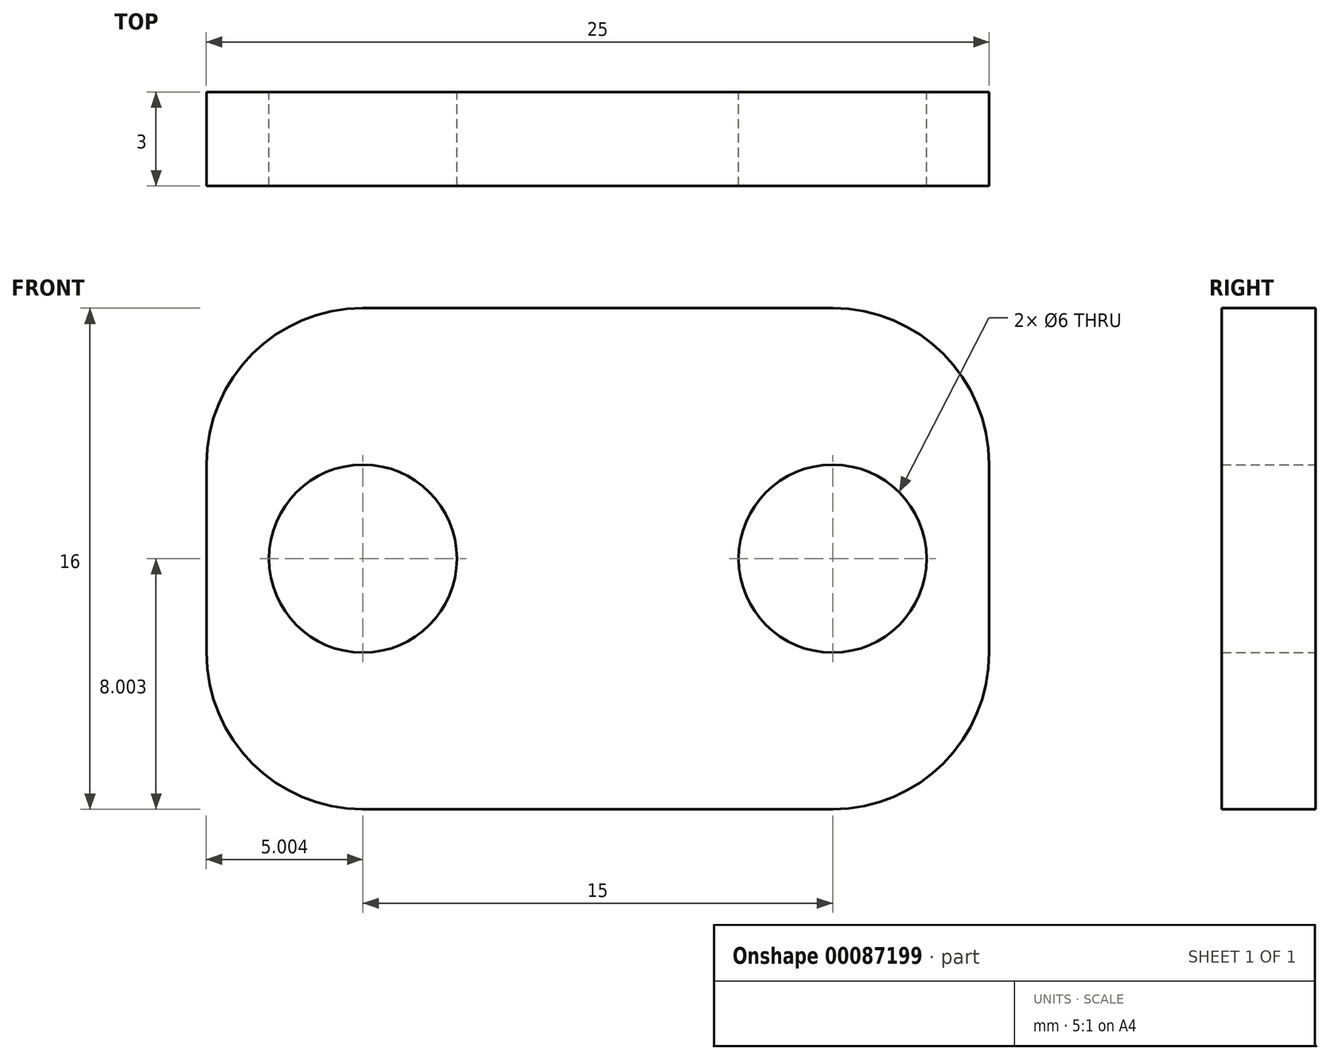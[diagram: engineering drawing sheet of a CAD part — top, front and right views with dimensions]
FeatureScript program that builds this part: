
annotation { "Feature Type Name" : "Feature", "Feature Type Description" : "" }
export const myFeature = defineFeature(function(context is Context, id is Id, definition is map)
    precondition{}
    {
        {
            var Q0;
            Q0=qCreatedBy(makeId("Front.planeOp"),FACE);
            var sketch = newSketch(context, id + "F0", { "sketchPlane" : qUnion([Q0])});
            skLineSegment(sketch, "E0", {"start": v(-155.44, 33.38) * mm, "end": v(-140.44, 33.38) * mm, "construction": true});
            skCircle(sketch, "E1", {"center": v(-155.44, 33.38) * mm, "radius": 3 * mm});
            skCircle(sketch, "E2", {"center": v(-140.44, 33.38) * mm, "radius": 3 * mm});
            skLineSegment(sketch, "E3.bottom", {"start": v(-140.44, 41.38) * mm, "end": v(-155.44, 41.38) * mm});
            skLineSegment(sketch, "E3.top", {"start": v(-140.44, 25.38) * mm, "end": v(-155.44, 25.38) * mm});
            skLineSegment(sketch, "E3.left", {"start": v(-135.44, 36.38) * mm, "end": v(-135.44, 30.38) * mm});
            skLineSegment(sketch, "E3.right", {"start": v(-160.44, 36.38) * mm, "end": v(-160.44, 30.38) * mm});
            skPoint(sketch, "E3.middle", {"position": v(-147.94, 33.38) * mm});
            skPoint(sketch, "E4.visualSharp", {"position": v(-135.44, 41.38) * mm});
            skArc(sketch, "E4.filletArc", {"start": v(-135.44, 36.38) * mm, "mid": v(-136.9, 39.92) * mm, "end": v(-140.44, 41.38) * mm});
            skPoint(sketch, "E5.visualSharp", {"position": v(-135.44, 25.38) * mm});
            skArc(sketch, "E5.filletArc", {"start": v(-140.44, 25.38) * mm, "mid": v(-136.9, 26.85) * mm, "end": v(-135.44, 30.38) * mm});
            skPoint(sketch, "E6.visualSharp", {"position": v(-160.44, 25.38) * mm});
            skArc(sketch, "E6.filletArc", {"start": v(-160.44, 30.38) * mm, "mid": v(-158.97, 26.85) * mm, "end": v(-155.44, 25.38) * mm});
            skPoint(sketch, "E7.visualSharp", {"position": v(-160.44, 41.38) * mm});
            skArc(sketch, "E7.filletArc", {"start": v(-155.44, 41.38) * mm, "mid": v(-158.97, 39.92) * mm, "end": v(-160.44, 36.38) * mm});
            skSolve(sketch);
        }
        {
            var Q0;
            Q0=qSketchRegion(id+"F0",true);
            extrude(context, id + "F1", {"entities" : qUnion([Q0]), "depth" : 3 * mm});
        }
    });
